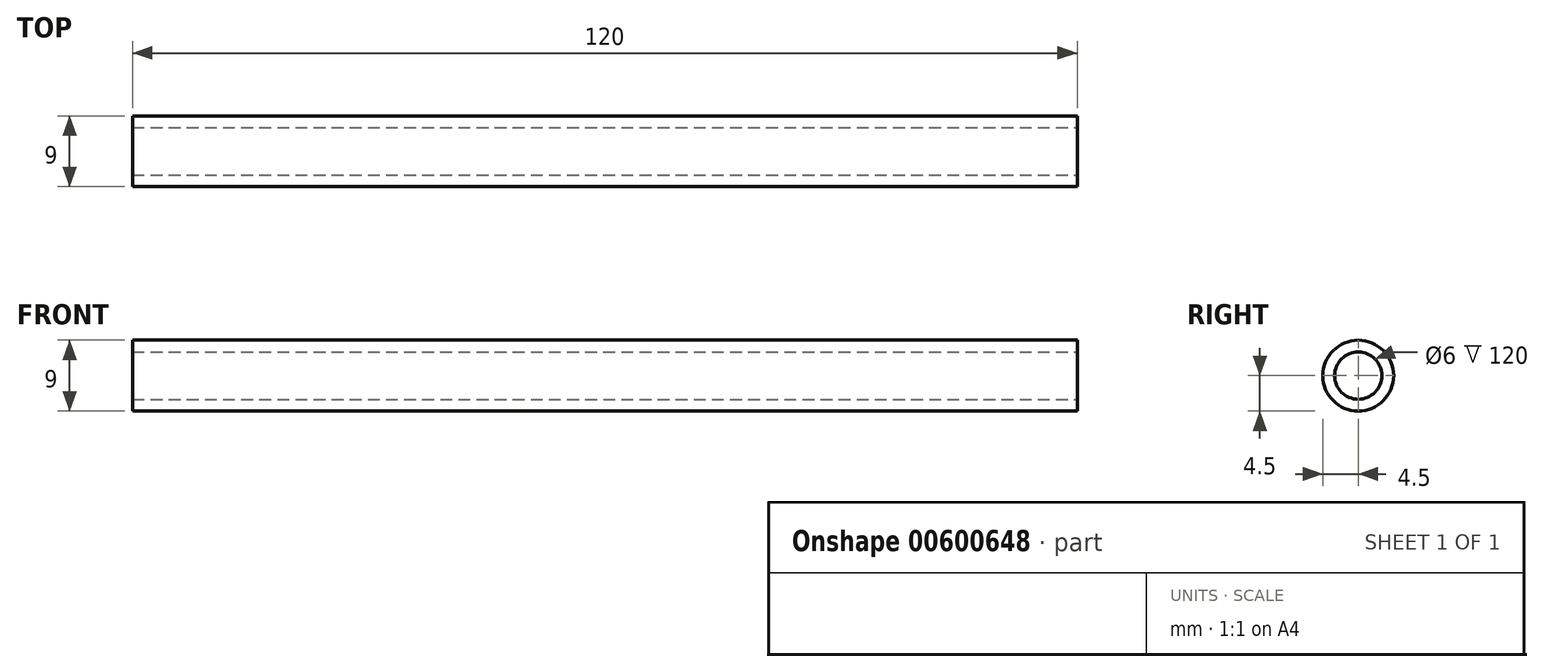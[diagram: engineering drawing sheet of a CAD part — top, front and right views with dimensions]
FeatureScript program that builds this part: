
annotation { "Feature Type Name" : "Feature", "Feature Type Description" : "" }
export const myFeature = defineFeature(function(context is Context, id is Id, definition is map)
    precondition{}
    {
        {
            var Q0;
            Q0=qCreatedBy(makeId("Right.planeOp"),FACE);
            var sketch = newSketch(context, id + "F0", { "sketchPlane" : qUnion([Q0])});
            skCircle(sketch, "E0", {"center": v(0, 0) * mm, "radius": 3 * mm});
            skCircle(sketch, "E1", {"center": v(0, 0) * mm, "radius": 4.5 * mm});
            skSolve(sketch);
        }
        {
            var Q0;
            Q0=makeQuery(id+"F0.imprint","IMPRINT",FACE,{"disambiguationData":[TD([[makeQuery(id+"F0.imprint","IMPRINT",EDGE,{"derivedFrom":sQuery(id+"F0.wireOp",EDGE,"E0")}),-1.0]])]});
            extrude(context, id + "F1", {"entities" : qUnion([Q0]), "oppositeDirection" : true, "depth" : 120 * mm, "offsetDistance" : 25 * mm});
        }
    });
